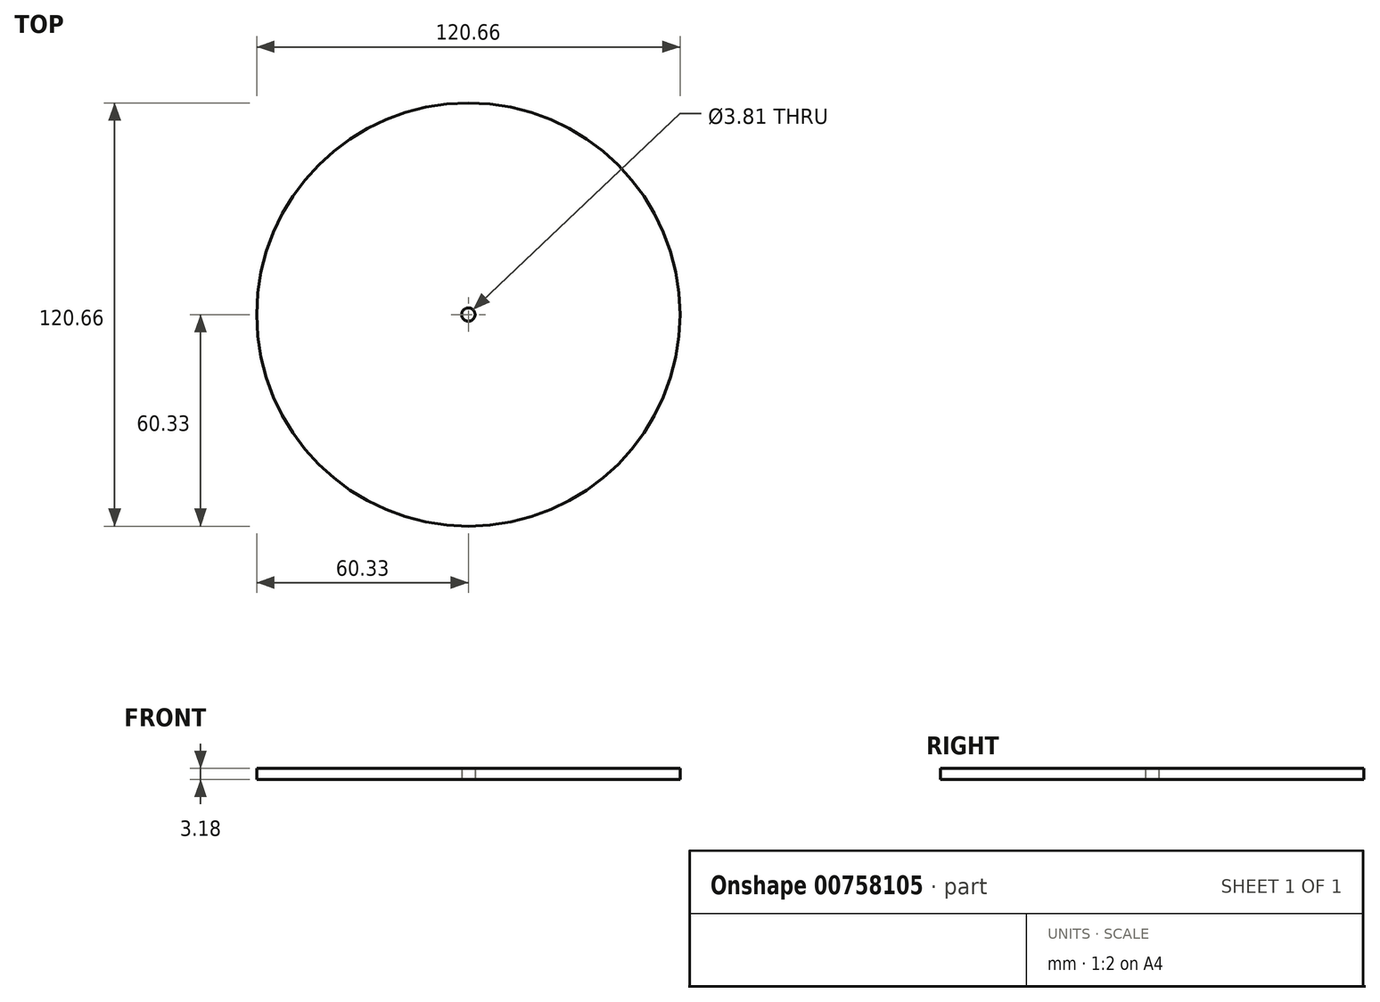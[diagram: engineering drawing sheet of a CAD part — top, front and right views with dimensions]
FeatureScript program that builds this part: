
annotation { "Feature Type Name" : "Feature", "Feature Type Description" : "" }
export const myFeature = defineFeature(function(context is Context, id is Id, definition is map)
    precondition{}
    {
        {
            var Q0;
            Q0=qCreatedBy(makeId("Top.planeOp"),FACE);
            var sketch = newSketch(context, id + "F0", { "sketchPlane" : qUnion([Q0])});
            skCircle(sketch, "E0", {"center": v(0, 0) * mm, "radius": 60.33 * mm});
            skCircle(sketch, "E1", {"center": v(0, 0) * mm, "radius": 1.9 * mm});
            skSolve(sketch);
        }
        {
            var Q0;
            Q0=makeQuery(id+"F0.imprint","IMPRINT",FACE,{"disambiguationData":[TD([[makeQuery(id+"F0.imprint","IMPRINT",EDGE,{"derivedFrom":sQuery(id+"F0.wireOp",EDGE,"E0")}),1.0]])]});
            extrude(context, id + "F1", {"entities" : qUnion([Q0]), "depth" : 3.17 * mm, "offsetDistance" : 25.4 * mm});
        }
    });
